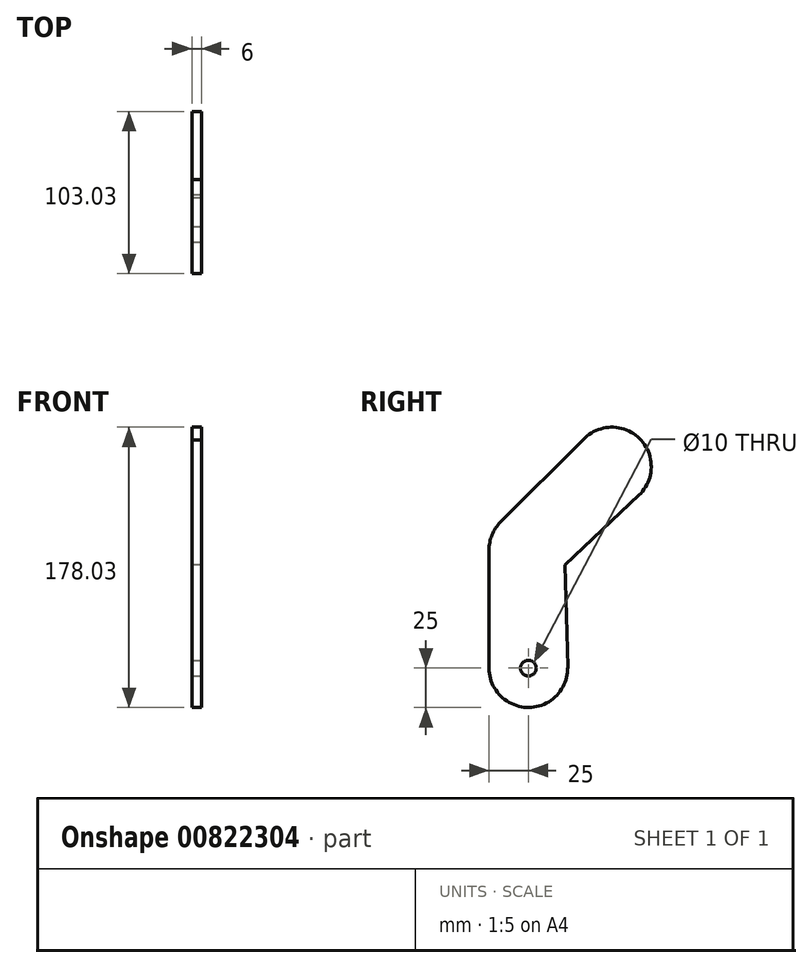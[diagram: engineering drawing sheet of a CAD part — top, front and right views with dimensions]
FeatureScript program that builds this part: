
annotation { "Feature Type Name" : "Feature", "Feature Type Description" : "" }
export const myFeature = defineFeature(function(context is Context, id is Id, definition is map)
    precondition{}
    {
        {
            var Q0;
            Q0=qCreatedBy(makeId("Right.planeOp"),FACE);
            var sketch = newSketch(context, id + "F0", { "sketchPlane" : qUnion([Q0])});
            skCircle(sketch, "E0", {"center": v(0, 0) * mm, "radius": 25 * mm});
            skLineSegment(sketch, "E1", {"start": v(0, 0) * mm, "end": v(0, 75) * mm});
            skLineSegment(sketch, "E2", {"start": v(0, 75) * mm, "end": v(53.03, 128.03) * mm});
            skCircle(sketch, "E3", {"center": v(53.03, 128.03) * mm, "radius": 25 * mm});
            skCircle(sketch, "E4", {"center": v(0, 75) * mm, "radius": 25 * mm});
            skLineSegment(sketch, "E5", {"start": v(-25, 0) * mm, "end": v(-25, 75) * mm});
            skLineSegment(sketch, "E6", {"start": v(0, 75) * mm, "end": v(55.77, 51.9) * mm});
            skLineSegment(sketch, "E7", {"start": v(23.1, 65.43) * mm, "end": v(24.99, 0.73) * mm});
            skLineSegment(sketch, "E8", {"start": v(23.1, 65.43) * mm, "end": v(70.19, 109.85) * mm});
            skLineSegment(sketch, "E9", {"start": v(34.73, 145.06) * mm, "end": v(-17.67, 92.68) * mm});
            skSolve(sketch);
        }
        {
            var Q0;
            Q0 = qSketchRegion(id + "F0", true);
            extrude(context, id + "F1", {"entities" : qUnion([Q0]), "depth" : 6 * mm, "offsetDistance" : 25 * mm});
        }
        {
            var Q0;
            Q0=makeQuery(id+"F1.opExtrude","CAP_FACE",FACE,{"disambiguationData":[OSD([sQuery(id+"F0.wireOp",EDGE,"E0"),sQuery(id+"F0.wireOp",EDGE,"E3"),sQuery(id+"F0.wireOp",EDGE,"E4"),sQuery(id+"F0.wireOp",EDGE,"E5"),sQuery(id+"F0.wireOp",EDGE,"E7"),sQuery(id+"F0.wireOp",EDGE,"E8"),sQuery(id+"F0.wireOp",EDGE,"E9")])],"isStart":false});
            var sketch = newSketch(context, id + "F2", { "sketchPlane" : qUnion([Q0])});
            skCircle(sketch, "E10", {"center": v(0, 0) * mm, "radius": 5 * mm});
            skSolve(sketch);
        }
        {
            var Q0;
            Q0 = qSketchRegion(id + "F2", true);
            extrude(context, id + "F3", {"entities" : qUnion([Q0]), "operationType" : NewBodyOperationType.REMOVE, "oppositeDirection" : true, "depth" : 6 * mm, "offsetDistance" : 25 * mm});
        }
    });
